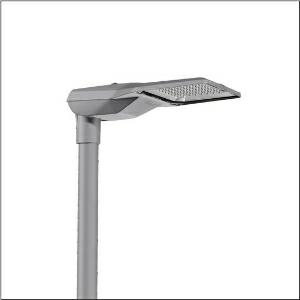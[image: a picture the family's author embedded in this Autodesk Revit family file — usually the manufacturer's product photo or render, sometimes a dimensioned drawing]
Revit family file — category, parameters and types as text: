
# Revit family: streetlight_sl_21_midi___st0_8a_5xe3c43s08nb_570f
name_source: partatom
category: Lighting Fixtures
units: mm (PartAtom-declared; Revit-internal decimal feet)

## family parameters
Cut with Voids When Loaded = No
Host = Face
Light Source = No
Part Type = Normal
Room Calculation Point = No
Round Connector Dimension = Use Diameter
Shared = No

## types (1)
- --- (1 x LED, 23710 lm, 151.2 W, 4000K)
    Apparent Load = 151 VA
    CIE Flux Codes = 41 75 97 100 100
    Color Rendering = 70
    Color Temperature = 4000K
    Default Elevation = 1800 mm
    Description = Streetlight SL 21 midi, mast luminaire, primary light control with lens, of PMMA, primary optical cover: cover, of toughened safety glass, transparent, light distribution: ST0.8a, light emission: direct distribution, primary light characteristic: asymmetric, installation type: side-entry, post-top, LED, High Power LED, rated luminous flux: 23.710lm, luminous efficacy: 157lm/W, light colour: 740, colour temperature: 4000K, control gear: D4i, control: overheat protection, constant luminous flux control, time-dependent luminous flux control, flexible luminous flux parameterisation, pre-setting: logarithmic dimming characteristic, mains connection: 230..240V, AC, 50/60Hz, start of lifetime: 151W, end of service life: 157W, reduction: 70W, luminaire housing, of diecast aluminium, powder-coated, SITECO metallic grey (DB 702S), corrosivity category C5 high according to DIN EN ISO 12944, please order mast flange separately, inclination adjustable: 0°, 5°, 10°, 15°, sealing non-destructively replaceable, multi-level sealing system, length: 644mm, width: 335mm, height: 110mm, mast flange for spigot size: 42mm (side-entry): 5XC10008XM4, 60/48mm (side-entry/post-top): 5XC10108XM2, 76/60mm (side-entry/post-top): 5XC10108XM1, mounting height: 4..8m, Smart Interface above, protection rating (complete): IP66, insulation class (complete): insulation class II (safety insulation), certification: CE, ENEC, ENEC+, VDE, impact resistance: IK10, permissible operating ambient temperature for outdoor applications: -40..+50°C, standard-compliant lighting for roads and squares, packaging unit: 1 piece

Light Distribution: ST0.8a
    Height = 111 mm
    Lamp = 1 x LED
    Lamp Light Flux = 23710 lm
    Lamp Power = 151.2 W
    Lamp count = 1
    Length = 644 mm
    Luminous efficacy = 157 lm/W
    Manufacturer = Siteco
    ModVariant = No
    Model = 5XE3C43S08NB
    Number of Poles = 1
    OnlyDefault = Yes
    Power Factor = 1
    Product Name = Streetlight SL 21 midi | ST0.8a
    Product group = mast luminaire | pylon top
    ProductGroupID = 6100
    Protection Class = Protection class II
    Protection Degree = IP 66
    RLX_Detail_Level = 1
    RLX_Emergency_Light_Flux = 0 lm
    RLX_Emergency_Type = 0
    RLX_Emergency_Type_DB = No
    RlxData = <blob elided: 26917 chars, md5=8ef1d7ac>
    Socket = socket
    Standby Power = 0 W
    System Light Flux = 23710 lm
    System Power = 151 W
    Type Comments = factory setting: luminous flux: 100 % | dim-lin: 254 | 802 mA
    Type Image = l_1004302.jpg
    URL = http://relux.com
    VarID = @adj_168197
    Voltage = 0 V
    Weight = 0.00 kg
    Width = 336 mm

## geometry (parser evidence)
native form markers: Blend x4, Sweep x10
no freeform markers — native parametric forms only
